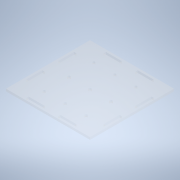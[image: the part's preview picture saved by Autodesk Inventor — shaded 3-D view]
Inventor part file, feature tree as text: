
AUTODESK INVENTOR PART (.ipt)
format: ipt  version: 2020 (Build 240168000, 168)  size: 186,368 bytes
history: native  units: mm
features: sketch x11, hole x9, extrude x2
ambient origin geometry x8: Origin, YZ Plane, XZ Plane, XY Plane, X Axis, Y Axis, Z Axis, Center Point
bodies: Solid1 (feature_tree)
feature tree (22):
  extrude  "Extrusion1"  Depth=106.0mm
  hole  "Hole1"  [1 undecoded]
  extrude  "Extrusion2"  Depth=1.0mm
  hole  "Hole2"  [1 undecoded]
  hole  "Hole3"  [1 undecoded]
  hole  "Hole4"  [1 undecoded]
  hole  "Hole5"  [1 undecoded]
  hole  "Hole6"  [1 undecoded]
  hole  "Hole7"  [1 undecoded]
  hole  "Hole8"  [1 undecoded]
  hole  "Hole9"  [1 undecoded]
  sketch  "Sketch1"  dims[d0=106.0mm d1=106.0mm]
  sketch  "Sketch2"  dims[d4=3.0mm d5=0.0mm d6=1.0mm]
  sketch  "Sketch3"  dims[d7=1.0mm d8=1.0mm]
  sketch  "Sketch5"  dims[d9=1.0mm d10=1.0mm]
  sketch  "Sketch6"  dims[d11=1.0mm d12=1.0mm]
  sketch  "Sketch7"  dims[d13=1.0mm d14=1.0mm]
  sketch  "Sketch8"  dims[d15=3.0mm d16=6.0mm d17=4.0mm d18=2.0mm d19=90.0deg d20=8.0mm d21=20.594885mm d22=112.0mm]
  sketch  "Sketch9"  dims[d23=112.0mm d24=3.0mm d25=0.0mm]
  sketch  "Sketch10"  dims[d26=3.0mm]
  sketch  "Sketch11"  dims[d27=3.0mm d28=6.0mm d29=4.0mm d30=2.0mm d31=90.0deg d32=8.0mm d33=20.594885mm d34=3.0mm]
  sketch  "Sketch12"  dims[d35=3.0mm d36=6.0mm d37=4.0mm d38=2.0mm d39=90.0deg d40=8.0mm d41=20.594885mm d42=3.0mm d43=3.0mm d44=6.0mm d45=4.0mm d46=2.0mm d47=90.0deg d48=8.0mm d49=20.594885mm d50=3.0mm d51=3.0mm d52=6.0mm d53=4.0mm d54=2.0mm d55=90.0deg d56=8.0mm d57=20.594885mm d58=3.0mm d59=3.0mm d60=6.0mm d61=4.0mm d62=2.0mm d63=90.0deg d64=8.0mm d65=20.594885mm d66=3.0mm d67=3.0mm d68=6.0mm d69=4.0mm d70=2.0mm d71=90.0deg d72=8.0mm d73=20.594885mm d74=3.0mm d75=3.0mm d76=6.0mm d77=4.0mm d78=2.0mm d79=90.0deg d80=8.0mm d81=20.594885mm d82=3.0mm d83=3.0mm d84=6.0mm d85=4.0mm d86=2.0mm d87=90.0deg d88=8.0mm d89=20.594885mm]
note: 9 required parameter values undecoded (feature->parameter linkage not recoverable at this tier; creation-order binding heuristic only, values carry confidence <= 0.55)
